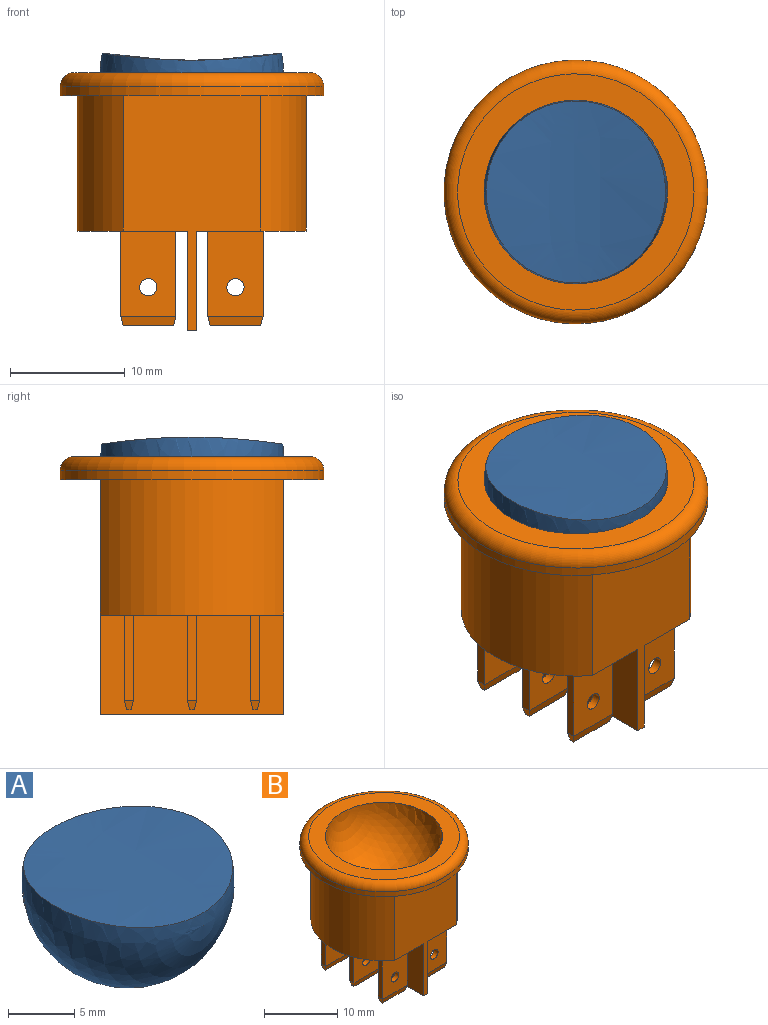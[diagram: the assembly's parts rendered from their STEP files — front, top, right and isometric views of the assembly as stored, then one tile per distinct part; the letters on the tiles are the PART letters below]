
ASSEMBLY  parts=2 mates=1
PART A: 2 faces, bbox 16x16x16 mm
  f0: sphere r=8mm, area 472.4mm2, adj f1
  f1: extruded ~15.85x15.64mm, area 195.3mm2, adj f0
PART B: 74 faces, bbox 24.9x24.9x22.5 mm
  f0: plane 16x9.6mm, normal (0,0,-1), area 122.8mm2, adj f5,f6,f8,f10,f43,f44,f45,f46
  f1: plane 23x23mm, normal (0,0,-1), area 134mm2, adj f2,f5,f6,f7,f8
  f2: cylinder r=11.5mm len=23mm, axis (0,0,-1), area 57.8mm2, adj f1,f4
  f3: plane 20.6x20.6mm, normal (0,0,1), area 132.2mm2, adj f4,f73
  f4: torus R=10.3mm, axis (0,0,1), area 131mm2, adj f2,f3
  f5: cylinder r=10mm len=16mm, axis (0,0,1), area 218.8mm2, adj f0,f1,f6,f8
  f6: plane 20.5x12mm, normal (0,-1,0), area 148.6mm2, adj f0,f1,f5,f7,f9,f10,f11,f12
  f7: cylinder r=10mm len=16mm, axis (0,0,1), area 218.8mm2, adj f1,f6,f8,f9
  f8: plane 20.5x12mm, normal (0,1,0), area 148.6mm2, adj f0,f1,f5,f7,f9,f10,f11,f12
  f9: plane 16x9.6mm, normal (0,0,-1), area 122.8mm2, adj f6,f7,f8,f11,f13,f14,f15,f16
  f10: plane 16x8.7mm, normal (1,0,0), area 139.2mm2, adj f0,f6,f8,f12
  f11: plane 16x8.7mm, normal (-1,0,0), area 139.2mm2, adj f6,f8,f9,f12
  f12: plane 16x0.8mm, normal (0,0,-1), area 12.8mm2, adj f6,f8,f10,f11
  f13: plane 7.45x4.8mm, normal (0,1,0), area 34mm2, adj f9,f14,f16,f20,f22
  f14: plane 7.45x0.8mm, normal (1,0,0), area 6mm2, adj f9,f13,f15,f18
  f15: plane 7.45x4.8mm, normal (0,-1,0), area 34mm2, adj f9,f14,f16,f19,f22
  f16: plane 7.45x0.8mm, normal (-1,0,0), area 6mm2, adj f9,f13,f15,f21
  f17: plane 4.4x0.4mm, normal (0,0,-1), area 1.8mm2, adj f18,f19,f20,f21
  f18: plane 0.8x0.8mm, normal (0.97,0,-0.24), area 0.5mm2, adj f14,f17,f19,f20
  f19: plane 4.8x0.8mm, normal (0,-0.97,-0.24), area 3.8mm2, adj f15,f17,f18,f21
  f20: plane 4.8x0.8mm, normal (0,0.97,-0.24), area 3.8mm2, adj f13,f17,f18,f21
  f21: plane 0.8x0.8mm, normal (-0.97,0,-0.24), area 0.5mm2, adj f16,f17,f19,f20
  f22: cylinder r=0.75mm len=1.5mm, axis (0,1,0), area 3.8mm2, adj f13,f15
  f23: plane 7.45x4.8mm, normal (0,1,0), area 34mm2, adj f9,f24,f26,f30,f32
  f24: plane 7.45x0.8mm, normal (1,0,0), area 6mm2, adj f9,f23,f25,f28
  f25: plane 7.45x4.8mm, normal (0,-1,0), area 34mm2, adj f9,f24,f26,f29,f32
  f26: plane 7.45x0.8mm, normal (-1,0,0), area 6mm2, adj f9,f23,f25,f31
  f27: plane 4.4x0.4mm, normal (0,0,-1), area 1.8mm2, adj f28,f29,f30,f31
  f28: plane 0.8x0.8mm, normal (0.97,0,-0.24), area 0.5mm2, adj f24,f27,f29,f30
  f29: plane 4.8x0.8mm, normal (0,-0.97,-0.24), area 3.8mm2, adj f25,f27,f28,f31
  f30: plane 4.8x0.8mm, normal (0,0.97,-0.24), area 3.8mm2, adj f23,f27,f28,f31
  f31: plane 0.8x0.8mm, normal (-0.97,0,-0.24), area 0.5mm2, adj f26,f27,f29,f30
  f32: cylinder r=0.75mm len=1.5mm, axis (0,1,0), area 3.8mm2, adj f23,f25
  f33: plane 7.45x4.8mm, normal (0,1,0), area 34mm2, adj f9,f34,f36,f40,f42
  f34: plane 7.45x0.8mm, normal (1,0,0), area 6mm2, adj f9,f33,f35,f38
  f35: plane 7.45x4.8mm, normal (0,-1,0), area 34mm2, adj f9,f34,f36,f39,f42
  f36: plane 7.45x0.8mm, normal (-1,0,0), area 6mm2, adj f9,f33,f35,f41
  f37: plane 4.4x0.4mm, normal (0,0,-1), area 1.8mm2, adj f38,f39,f40,f41
  f38: plane 0.8x0.8mm, normal (0.97,0,-0.24), area 0.5mm2, adj f34,f37,f39,f40
  f39: plane 4.8x0.8mm, normal (0,-0.97,-0.24), area 3.8mm2, adj f35,f37,f38,f41
  f40: plane 4.8x0.8mm, normal (0,0.97,-0.24), area 3.8mm2, adj f33,f37,f38,f41
  f41: plane 0.8x0.8mm, normal (-0.97,0,-0.24), area 0.5mm2, adj f36,f37,f39,f40
  f42: cylinder r=0.75mm len=1.5mm, axis (0,1,0), area 3.8mm2, adj f33,f35
  f43: plane 7.45x4.8mm, normal (0,1,0), area 34mm2, adj f0,f44,f46,f50,f52
  f44: plane 7.45x0.8mm, normal (1,0,0), area 6mm2, adj f0,f43,f45,f48
  f45: plane 7.45x4.8mm, normal (0,-1,0), area 34mm2, adj f0,f44,f46,f49,f52
  f46: plane 7.45x0.8mm, normal (-1,0,0), area 6mm2, adj f0,f43,f45,f51
  f47: plane 4.4x0.4mm, normal (0,0,-1), area 1.8mm2, adj f48,f49,f50,f51
  f48: plane 0.8x0.8mm, normal (0.97,0,-0.24), area 0.5mm2, adj f44,f47,f49,f50
  f49: plane 4.8x0.8mm, normal (0,-0.97,-0.24), area 3.8mm2, adj f45,f47,f48,f51
  f50: plane 4.8x0.8mm, normal (0,0.97,-0.24), area 3.8mm2, adj f43,f47,f48,f51
  f51: plane 0.8x0.8mm, normal (-0.97,0,-0.24), area 0.5mm2, adj f46,f47,f49,f50
  f52: cylinder r=0.75mm len=1.5mm, axis (0,1,0), area 3.8mm2, adj f43,f45
  f53: plane 7.45x4.8mm, normal (0,1,0), area 34mm2, adj f0,f54,f56,f60,f62
  f54: plane 7.45x0.8mm, normal (1,0,0), area 6mm2, adj f0,f53,f55,f58
  f55: plane 7.45x4.8mm, normal (0,-1,0), area 34mm2, adj f0,f54,f56,f59,f62
  f56: plane 7.45x0.8mm, normal (-1,0,0), area 6mm2, adj f0,f53,f55,f61
  f57: plane 4.4x0.4mm, normal (0,0,-1), area 1.8mm2, adj f58,f59,f60,f61
  f58: plane 0.8x0.8mm, normal (0.97,0,-0.24), area 0.5mm2, adj f54,f57,f59,f60
  f59: plane 4.8x0.8mm, normal (0,-0.97,-0.24), area 3.8mm2, adj f55,f57,f58,f61
  f60: plane 4.8x0.8mm, normal (0,0.97,-0.24), area 3.8mm2, adj f53,f57,f58,f61
  f61: plane 0.8x0.8mm, normal (-0.97,0,-0.24), area 0.5mm2, adj f56,f57,f59,f60
  f62: cylinder r=0.75mm len=1.5mm, axis (0,1,0), area 3.8mm2, adj f53,f55
  f63: plane 7.45x4.8mm, normal (0,1,0), area 34mm2, adj f0,f64,f66,f70,f72
  f64: plane 7.45x0.8mm, normal (1,0,0), area 6mm2, adj f0,f63,f65,f68
  f65: plane 7.45x4.8mm, normal (0,-1,0), area 34mm2, adj f0,f64,f66,f69,f72
  f66: plane 7.45x0.8mm, normal (-1,0,0), area 6mm2, adj f0,f63,f65,f71
  f67: plane 4.4x0.4mm, normal (0,0,-1), area 1.8mm2, adj f68,f69,f70,f71
  f68: plane 0.8x0.8mm, normal (0.97,0,-0.24), area 0.5mm2, adj f64,f67,f69,f70
  f69: plane 4.8x0.8mm, normal (0,-0.97,-0.24), area 3.8mm2, adj f65,f67,f68,f71
  f70: plane 4.8x0.8mm, normal (0,0.97,-0.24), area 3.8mm2, adj f63,f67,f68,f71
  f71: plane 0.8x0.8mm, normal (-0.97,0,-0.24), area 0.5mm2, adj f66,f67,f69,f70
  f72: cylinder r=0.75mm len=1.5mm, axis (0,1,0), area 3.8mm2, adj f63,f65
  f73: sphere r=8mm, area 402.1mm2, adj f3
PLACE A at identity
PLACE B at identity fixed
MATE fastened B.f5 <-> A.f0  axis (0,0,1) through (0,0,2)mm
